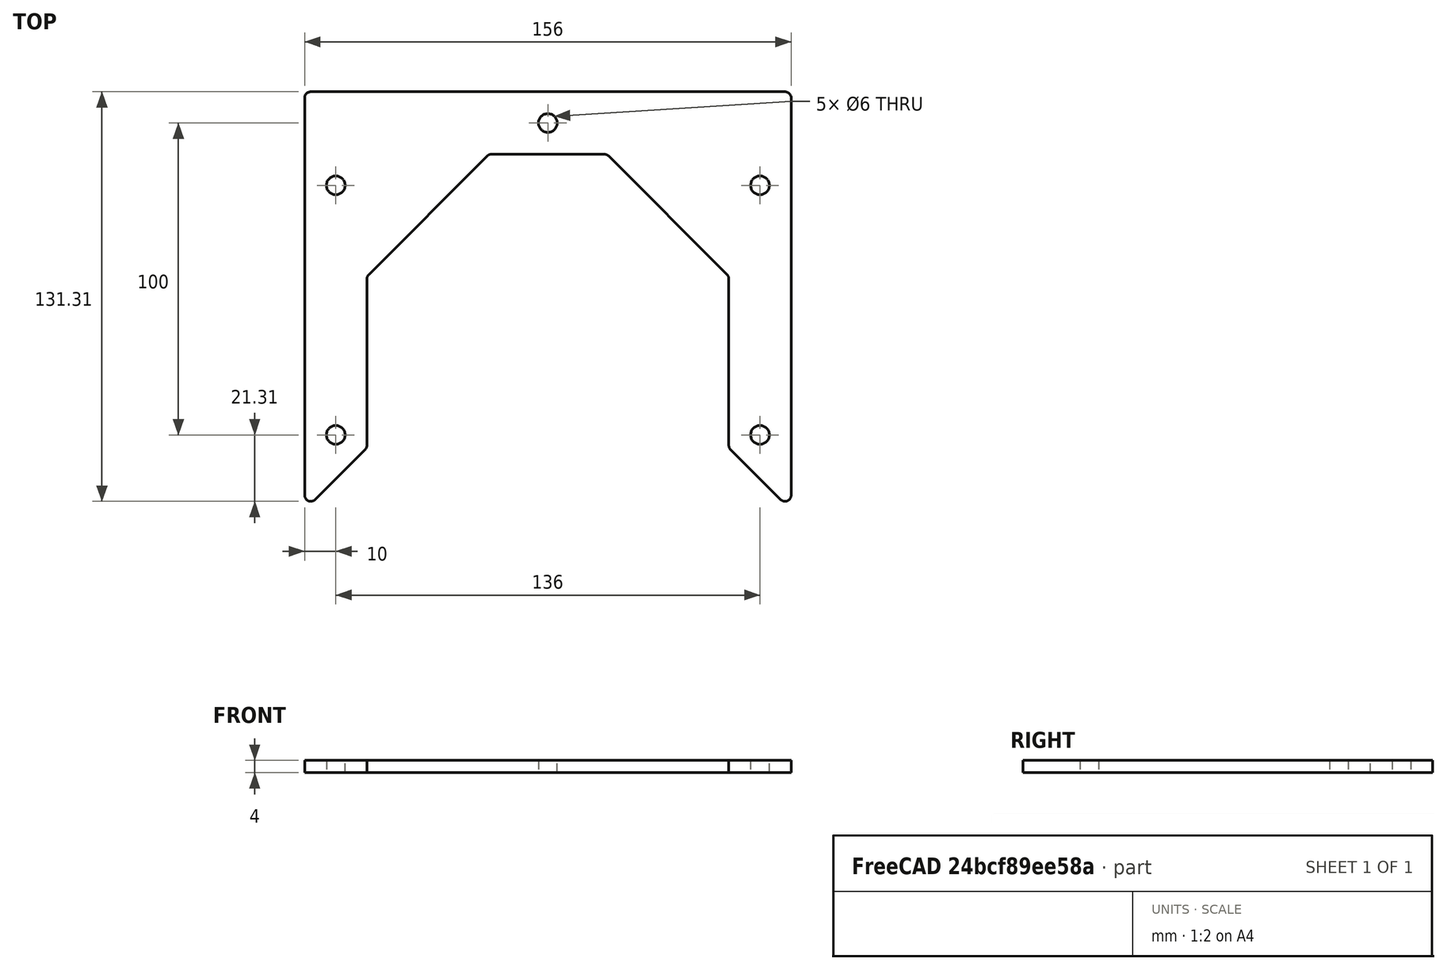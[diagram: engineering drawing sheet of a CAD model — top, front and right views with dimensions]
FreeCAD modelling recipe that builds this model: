
FCSTD DOCUMENT  (FreeCAD 0.19R24267 +99 (Git))
Label: V2 Enclosure ends U bracket without rail end holes
License: All rights reserved
LicenseURL: http://en.wikipedia.org/wiki/All_rights_reserved
objects: Sketcher::SketchObject×1, PartDesign::Pad×1, PartDesign::Body×1
note: 4 computed .brp shape members not serialized (recipe doc carries the construction recipe); baked Part::Feature solids carry a one-line shape summary decoded from their .brp

FEATURE [Sketcher::SketchObject] Sketch
  FullyConstrained = true
  MapMode = 5
  Support = -> [XY_Plane]
  sketch-geometry (31):
    g0: LineSegment StartX=-68 StartY=0 StartZ=0 EndX=-68 EndY=-114.142 EndZ=0
    g1: Circle CenterX=-68 CenterY=-20 CenterZ=0 NormalX=0 NormalY=0 NormalZ=1 AngleXU=0 Radius=3
    g2: Circle CenterX=-68 CenterY=-100 CenterZ=0 NormalX=0 NormalY=0 NormalZ=1 AngleXU=0 Radius=3
    g3: LineSegment StartX=68 StartY=0 StartZ=0 EndX=68 EndY=-114.142 EndZ=0
    g4: Circle CenterX=68 CenterY=-20 CenterZ=0 NormalX=0 NormalY=0 NormalZ=1 AngleXU=0 Radius=3
    g5: Circle CenterX=68 CenterY=-100 CenterZ=0 NormalX=0 NormalY=0 NormalZ=1 AngleXU=0 Radius=3
    g6: LineSegment StartX=-78 StartY=8 StartZ=0 EndX=-78 EndY=-119.314 EndZ=0
    g7: LineSegment StartX=-58 StartY=-50 StartZ=0 EndX=-58 EndY=-103.314 EndZ=0
    g8: LineSegment StartX=-57.4142 StartY=-48.5858 StartZ=0 EndX=-19.4142 EndY=-10.5858 EndZ=0
    g9: LineSegment StartX=-18 StartY=-10 StartZ=0 EndX=18 EndY=-10 EndZ=0
    g10: LineSegment StartX=19.4142 StartY=-10.5858 StartZ=0 EndX=57.4142 EndY=-48.5858 EndZ=0
    g11: LineSegment StartX=58 StartY=-50 StartZ=0 EndX=58 EndY=-103.314 EndZ=0
    g12: LineSegment StartX=58.5858 StartY=-104.728 StartZ=0 EndX=74.5858 EndY=-120.728 EndZ=0
    g13: LineSegment StartX=78 StartY=-119.314 StartZ=0 EndX=78 EndY=8 EndZ=0
    g14: LineSegment StartX=76 StartY=10 StartZ=0 EndX=-76 EndY=10 EndZ=0
    g15: LineSegment StartX=-74.5858 StartY=-120.728 StartZ=0 EndX=-58.5858 EndY=-104.728 EndZ=0
    g16: ArcOfCircle CenterX=-76 CenterY=8 CenterZ=0 NormalX=0 NormalY=0 NormalZ=1 AngleXU=0 Radius=2 StartAngle=1.5708 EndAngle=3.14159
    g17: ArcOfCircle CenterX=-76 CenterY=-119.314 CenterZ=0 NormalX=0 NormalY=0 NormalZ=1 AngleXU=0 Radius=2 StartAngle=3.14159 EndAngle=5.49779
    g18: ArcOfCircle CenterX=-60 CenterY=-103.314 CenterZ=0 NormalX=0 NormalY=0 NormalZ=1 AngleXU=0 Radius=2 StartAngle=5.49779 EndAngle=6.28319
    g19: ArcOfCircle CenterX=60 CenterY=-103.314 CenterZ=0 NormalX=0 NormalY=0 NormalZ=1 AngleXU=0 Radius=2 StartAngle=3.14159 EndAngle=3.92699
    g20: ArcOfCircle CenterX=76 CenterY=-119.314 CenterZ=0 NormalX=0 NormalY=0 NormalZ=1 AngleXU=0 Radius=2 StartAngle=3.92699 EndAngle=6.28319
    g21: ArcOfCircle CenterX=76 CenterY=8 CenterZ=0 NormalX=0 NormalY=0 NormalZ=1 AngleXU=0 Radius=2 StartAngle=0 EndAngle=1.5708
    g22: ArcOfCircle CenterX=-56 CenterY=-50 CenterZ=0 NormalX=0 NormalY=0 NormalZ=1 AngleXU=0 Radius=2 StartAngle=2.35619 EndAngle=3.14159
    g23: ArcOfCircle CenterX=-18 CenterY=-12 CenterZ=0 NormalX=0 NormalY=0 NormalZ=1 AngleXU=0 Radius=2 StartAngle=1.5708 EndAngle=2.35619
    g24: ArcOfCircle CenterX=18 CenterY=-12 CenterZ=0 NormalX=0 NormalY=0 NormalZ=1 AngleXU=0 Radius=2 StartAngle=0.785398 EndAngle=1.5708
    g25: ArcOfCircle CenterX=56 CenterY=-50 CenterZ=0 NormalX=0 NormalY=0 NormalZ=1 AngleXU=0 Radius=2 StartAngle=0 EndAngle=0.785398
    g26: Circle CenterX=-68 CenterY=-100 CenterZ=0 NormalX=0 NormalY=0 NormalZ=1 AngleXU=0 Radius=10
    g27: Circle CenterX=68 CenterY=-100 CenterZ=0 NormalX=0 NormalY=0 NormalZ=1 AngleXU=0 Radius=10
    g28: GeomPoint X=0 Y=-10 Z=0
    g29: GeomPoint X=0 Y=10 Z=0
    g30: Circle CenterX=0 CenterY=0 CenterZ=0 NormalX=0 NormalY=0 NormalZ=1 AngleXU=0 Radius=3
  constraints (72):
    c: Vertical(g0)
    c: PointOnObject(g1,g0)
    c: PointOnObject(g2,g0)
    c: Vertical(g3)
    c: Symmetric(g1,g4,g-2)
    c: Symmetric(g2,g5,g-2)
    c: Equal(g2,g1)
    c: Equal(g1,g4)
    c: Equal(g4,g5)
    c: Radius(g1) = 3
    c: Vertical(g6)
    c: Vertical(g7)
    c: Vertical(g13)
    c: Horizontal(g14)
    c: Tangent(g14,g16) = -1.5708
    c: Tangent(g6,g16) = -1.5708
    c: Tangent(g6,g17) = -1.5708
    c: Tangent(g15,g17) = -1.5708
    c: Tangent(g7,g18) = 1.5708
    c: Tangent(g15,g18) = -1.5708
    c: Tangent(g11,g19) = -1.5708
    c: Tangent(g12,g19) = -1.5708
    c: Tangent(g13,g20) = -1.5708
    c: Tangent(g12,g20) = -1.5708
    c: Tangent(g14,g21) = -1.5708
    c: Tangent(g13,g21) = -1.5708
    c: Tangent(g8,g22) = 1.5708
    c: Tangent(g7,g22) = -1.5708
    c: Tangent(g8,g23) = 1.5708
    c: Tangent(g9,g23) = 1.5708
    c: Tangent(g10,g24) = 1.5708
    c: Tangent(g9,g24) = 1.5708
    c: Tangent(g10,g25) = 1.5708
    c: Tangent(g11,g25) = 1.5708
    c: Equal(g16,g22)
    c: Equal(g22,g23)
    c: Equal(g23,g21)
    c: Equal(g21,g24)
    c: Equal(g24,g25)
    c: Equal(g25,g20)
    c: Equal(g20,g19)
    c: Equal(g19,g17)
    c: Equal(g17,g18)
    c: Radius(g16) = 2
    c: PointOnObject(g0,g15)
    c: PointOnObject(g3,g12)
    c: Coincident(g26,g2)
    c: Coincident(g27,g5)
    c: Tangent(g27,g13)
    c: Tangent(g27,g12)
    c: Tangent(g11,g27)
    c: Tangent(g6,g26)
    c: Angle(g15,g6) = 0.785398
    c: DistanceX(g7,g9) = 40
    c: DistanceY(g7,g9) = 40
    c: Symmetric(g9,g9,g-2)
    c: Symmetric(g7,g11,g-2)
    c: DistanceX(g6,g7) = 20
    c: Symmetric(g6,g13,g-2)
    c: Symmetric(g7,g11,g-2)
    c: PointOnObject(g28,g-2)
    c: PointOnObject(g28,g9)
    c: PointOnObject(g29,g14)
    c: Symmetric(g29,g28,g-1)
    c: DistanceY(g28,g29) = 20
    c: Coincident(g30,g-1)
    c: Equal(g30,g1)
    c: Symmetric(g0,g3,g30)
    c: DistanceX(g0,g3) = 136
    c: DistanceY(g1,g0) = 20
    c: DistanceY(g2,g0) = 100
    c: PointOnObject(g0,g-1)
FEATURE [PartDesign::Pad] Pad
  Direction = (1,1,1)
  Length = 4
  Length2 = 100
  Profile = -> Sketch
  Type = 0
FEATURE [PartDesign::Body] Body
  Group = -> [Sketch,Pad]
  Origin = -> Origin
  Tip = -> Pad
